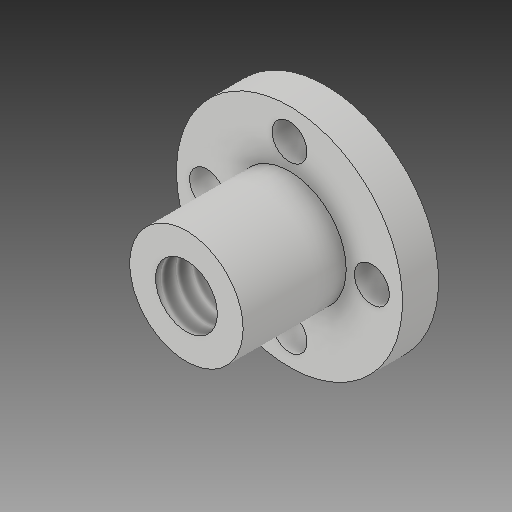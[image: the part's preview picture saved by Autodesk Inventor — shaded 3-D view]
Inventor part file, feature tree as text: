
AUTODESK INVENTOR PART (.ipt)
format: ipt  version: 2018 (Build 220112000, 112)  size: 151,040 bytes
history: native  units: mm
features: reference x5, extrude x3, sketch x3, other x3, thread x1
ambient origin geometry x8: Origin, YZ Plane, XZ Plane, XY Plane, X Axis, Y Axis, Z Axis, Center Point
bodies: Solid1 (feature_tree)
feature tree (15):
  extrude  "Extrusion1"  Depth=10.16mm
  extrude  "Extrusion2"  Depth=3.5mm
  extrude  "Extrusion3"  Depth=10.0mm TaperAngle=0.0deg
  thread  "Thread1"  [1 undecoded]
  sketch  "Sketch1"  dims[d0=21.93mm d1=10.16mm]
  reference  "Reference1"
  sketch  "Sketch2"  dims[d2=3.5mm d3=0.0mm d4=6.0mm]
  sketch  "Sketch3"  dims[d5=10.0mm d6=0.0mm d7=10.0mm d8=0.0mm d9=10.0mm d10=0.0mm]
  reference  "Reference2"
  reference  "Reference3"
  reference  "Reference4"
  reference  "Reference5"
  parser-record x1  (decoder bookkeeping rows leaked as tree rows — omitted from the tree; the rows remain in map.json)
  other  "Front-Bed-Holder.iam"
  other  "Left Bed Holder Mid:1"
note: 1 required parameter value undecoded (feature->parameter linkage not recoverable at this tier; creation-order binding heuristic only, values carry confidence <= 0.55)
note: 1 file-system path scrubbed to <path> (originals preserved in map.json)
